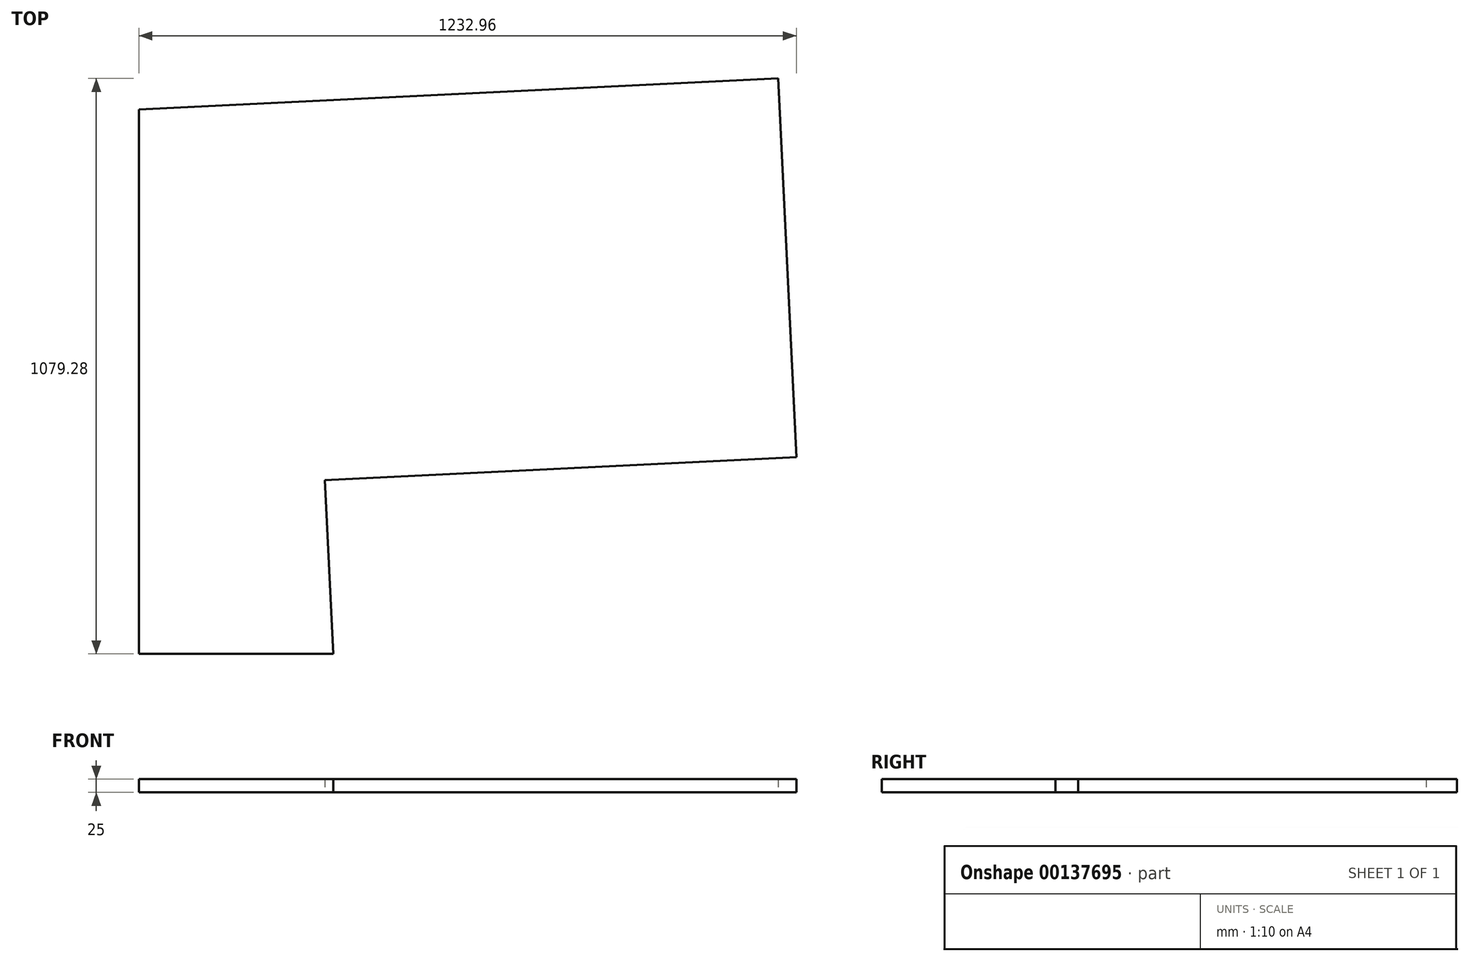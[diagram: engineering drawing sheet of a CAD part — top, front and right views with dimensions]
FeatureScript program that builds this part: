
annotation { "Feature Type Name" : "Feature", "Feature Type Description" : "" }
export const myFeature = defineFeature(function(context is Context, id is Id, definition is map)
    precondition{}
    {
        {
            var Q0;
            Q0=qCreatedBy(makeId("Top.planeOp"),FACE);
            var sketch = newSketch(context, id + "F0", { "sketchPlane" : qUnion([Q0])});
            skLineSegment(sketch, "E0", {"start": v(-549.76, -368.78) * mm, "end": v(-549.76, 652.54) * mm});
            skLineSegment(sketch, "E1", {"start": v(-549.76, 652.54) * mm, "end": v(648.84, 710.5) * mm});
            skLineSegment(sketch, "E2", {"start": v(648.84, 710.5) * mm, "end": v(683.2, 0) * mm});
            skLineSegment(sketch, "E3", {"start": v(683.2, 0) * mm, "end": v(-201.37, -42.77) * mm});
            skLineSegment(sketch, "E4", {"start": v(-201.37, -42.77) * mm, "end": v(-185.6, -368.78) * mm});
            skLineSegment(sketch, "E5", {"start": v(-185.6, -368.78) * mm, "end": v(-549.76, -368.78) * mm});
            skSolve(sketch);
        }
        {
            var Q0;
            Q0=makeQuery(id+"F0.imprint","IMPRINT",FACE,{"disambiguationData":[TD([[makeQuery(id+"F0.imprint","IMPRINT",EDGE,{"derivedFrom":sQuery(id+"F0.wireOp",EDGE,"E0")}),-1.0]])]});
            extrude(context, id + "F1", {"entities" : qUnion([Q0]), "depth" : 25 * mm});
        }
    });
